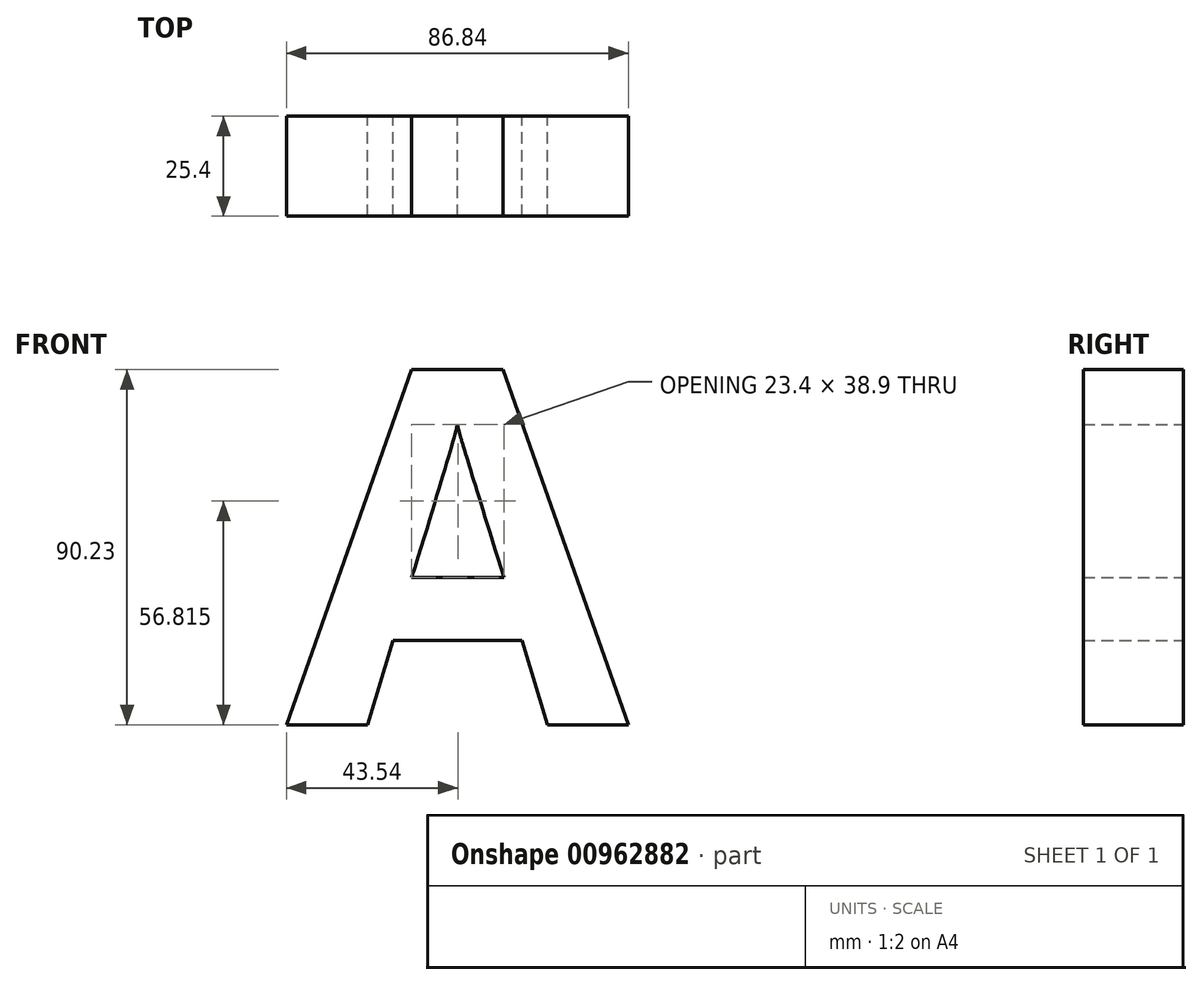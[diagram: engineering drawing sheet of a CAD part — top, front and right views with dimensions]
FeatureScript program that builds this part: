
annotation { "Feature Type Name" : "Feature", "Feature Type Description" : "" }
export const myFeature = defineFeature(function(context is Context, id is Id, definition is map)
    precondition{}
    {
        {
            var Q0;
            Q0=qCreatedBy(makeId("Front.planeOp"),FACE);
            var sketch = newSketch(context, id + "F0", { "sketchPlane" : qUnion([Q0])});
            skText(sketch, "E0", { "text": "A", "fontName": "OpenSans-Bold.ttf"});
            const initialGuessF0  = {"E0": [-0.0579, -0.04285, 1, 0, 0.09062]};
            skSetInitialGuess(sketch, initialGuessF0);
            skSolve(sketch);
        }
        {
            var Q0;
            Q0 = qSketchRegion(id + "F0", true);
            extrude(context, id + "F1", {"entities" : qUnion([Q0]), "depth" : 25.4 * mm, "offsetDistance" : 25.4 * mm});
        }
    });
